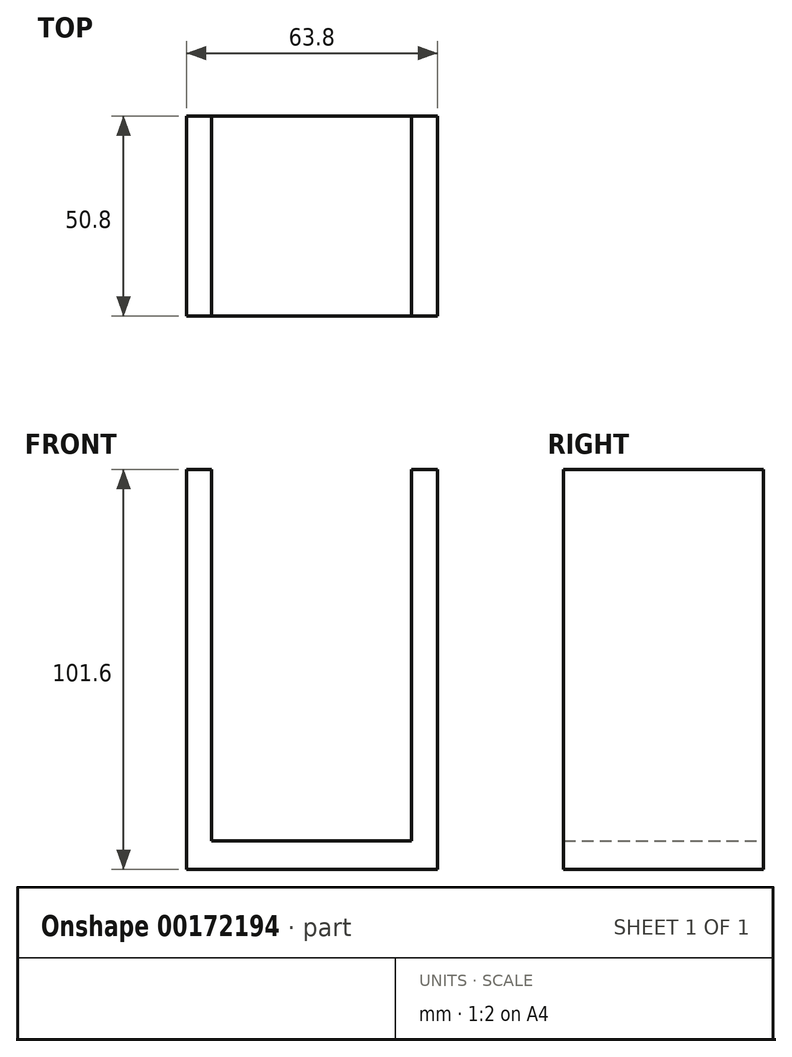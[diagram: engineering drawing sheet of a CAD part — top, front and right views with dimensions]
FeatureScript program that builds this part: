
annotation { "Feature Type Name" : "Feature", "Feature Type Description" : "" }
export const myFeature = defineFeature(function(context is Context, id is Id, definition is map)
    precondition{}
    {
        {
            var Q0;
            Q0=qCreatedBy(makeId("Front.planeOp"),FACE);
            var sketch = newSketch(context, id + "F0", { "sketchPlane" : qUnion([Q0])});
            skLineSegment(sketch, "E0.bottom", {"start": v(-63.8, 101.6) * mm, "end": v(-57.4, 101.6) * mm});
            skLineSegment(sketch, "E0.top", {"start": v(-63.8, 0) * mm, "end": v(-57.4, 0) * mm});
            skLineSegment(sketch, "E0.left", {"start": v(-63.8, 101.6) * mm, "end": v(-63.8, 0) * mm});
            skLineSegment(sketch, "E0.right", {"start": v(-57.4, 101.6) * mm, "end": v(-57.4, 0) * mm});
            skLineSegment(sketch, "E1.bottom", {"start": v(-63.8, 7.2) * mm, "end": v(0, 7.2) * mm});
            skLineSegment(sketch, "E1.top", {"start": v(-63.8, 0) * mm, "end": v(0, 0) * mm});
            skLineSegment(sketch, "E1.left", {"start": v(-63.8, 7.2) * mm, "end": v(-63.8, 0) * mm});
            skLineSegment(sketch, "E1.right", {"start": v(0, 7.2) * mm, "end": v(0, 0) * mm});
            skLineSegment(sketch, "E2.bottom", {"start": v(0, 0) * mm, "end": v(-6.6, 0) * mm});
            skLineSegment(sketch, "E2.top", {"start": v(0, 101.6) * mm, "end": v(-6.6, 101.6) * mm});
            skLineSegment(sketch, "E2.left", {"start": v(0, 0) * mm, "end": v(0, 101.6) * mm});
            skLineSegment(sketch, "E2.right", {"start": v(-6.6, 0) * mm, "end": v(-6.6, 101.6) * mm});
            skSolve(sketch);
        }
        {
            var Q0;
            Q0 = qSketchRegion(id + "F0", true);
            extrude(context, id + "F1", {"entities" : qUnion([Q0]), "depth" : 50.8 * mm});
        }
    });
